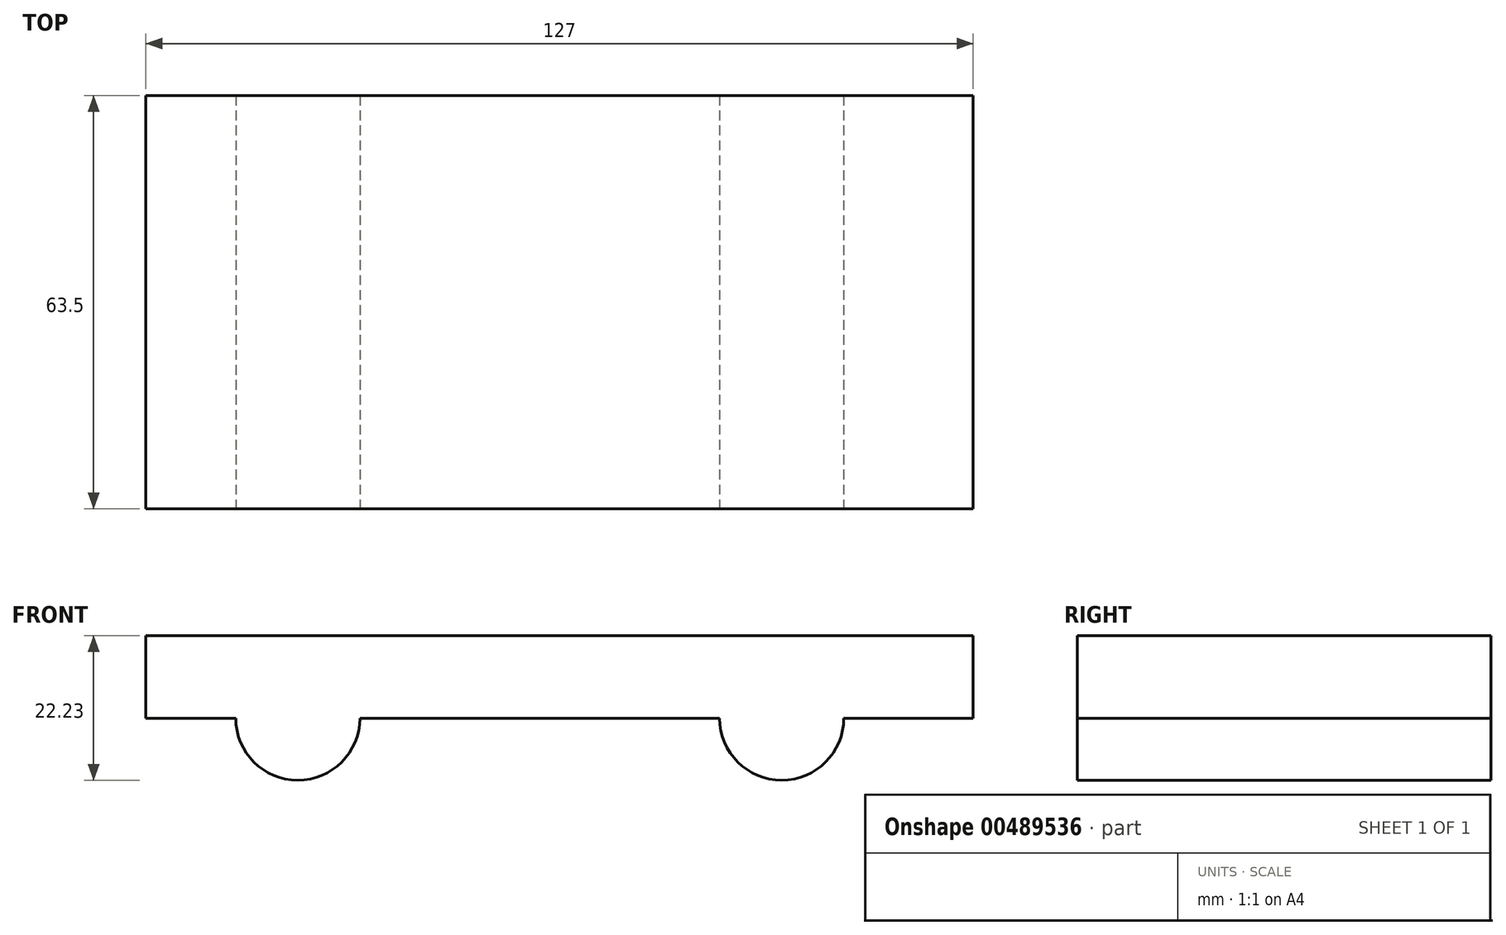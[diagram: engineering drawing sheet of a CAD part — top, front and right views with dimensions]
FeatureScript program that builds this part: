
annotation { "Feature Type Name" : "Feature", "Feature Type Description" : "" }
export const myFeature = defineFeature(function(context is Context, id is Id, definition is map)
    precondition{}
    {
        {
            var Q0;
            Q0=qCreatedBy(makeId("Top.planeOp"),FACE);
            var sketch = newSketch(context, id + "F0", { "sketchPlane" : qUnion([Q0])});
            skLineSegment(sketch, "E0.bottom", {"start": v(-63.5, 31.75) * mm, "end": v(63.5, 31.75) * mm});
            skLineSegment(sketch, "E0.top", {"start": v(-63.5, -31.75) * mm, "end": v(63.5, -31.75) * mm});
            skLineSegment(sketch, "E0.left", {"start": v(-63.5, 31.75) * mm, "end": v(-63.5, -31.75) * mm});
            skLineSegment(sketch, "E0.right", {"start": v(63.5, 31.75) * mm, "end": v(63.5, -31.75) * mm});
            skPoint(sketch, "E0.middle", {"position": v(0, 0) * mm});
            skSolve(sketch);
        }
        {
            var Q0;
            Q0=makeQuery(id+"F0.imprint","IMPRINT",FACE,{"disambiguationData":[TD([[makeQuery(id+"F0.imprint","IMPRINT",EDGE,{"derivedFrom":sQuery(id+"F0.wireOp",EDGE,"E0.bottom")}),-1.0]])]});
            extrude(context, id + "F1", {"entities" : qUnion([Q0]), "depth" : 12.7 * mm});
        }
        {
            var Q0;
            Q0=makeQuery(id+"F1.opExtrude","SWEPT_FACE",FACE,{"disambiguationData":[OSD([sQuery(id+"F0.wireOp",EDGE,"E0.top")])]});
            var sketch = newSketch(context, id + "F2", { "sketchPlane" : qUnion([Q0])});
            skCircle(sketch, "E1", {"center": v(-40.18, 0) * mm, "radius": 9.52 * mm});
            skSolve(sketch);
        }
        {
            var Q0;
            {var subQ0=sQuery(id+"F0.wireOp",EDGE,"E0.top");Q0=makeQuery(id+"F2.imprint","IMPRINT",FACE,{"disambiguationData":[TD([[makeQuery(id+"F2.imprint","IMPRINT",EDGE,{"derivedFrom":makeQuery(id+"F1.opExtrude","CAP_EDGE",EDGE,{"disambiguationData":[OSD([subQ0])],"isStart":false})}),-1.0]])]});}
            var sketch = newSketch(context, id + "F3", { "sketchPlane" : qUnion([Q0])});
            skCircle(sketch, "E2", {"center": v(34.1, 0) * mm, "radius": 9.53 * mm});
            skSolve(sketch);
        }
        {
            var Q0;
            {var subQ0=sQuery(id+"F2.wireOp",EDGE,"E1");var subQ1=makeQuery(id+"F1.opExtrude","CAP_EDGE",EDGE,{"disambiguationData":[OSD([sQuery(id+"F0.wireOp",EDGE,"E0.top")])],"isStart":true});var subQ2=makeQuery(id+"F2.imprint","INTERSECT",VERTEX,{"disambiguationData":[OD(0.0)],"derivedFrom":[subQ1,subQ0]});Q0=makeQuery(id+"F2.imprint","IMPRINT",FACE,{"disambiguationData":[TD([[makeQuery(id+"F2.imprint","IMPRINT",EDGE,{"disambiguationData":[TD([[subQ2,-1.0]])],"derivedFrom":subQ0}),1.0]])]});}
            var Q1;
            {var subQ0=sQuery(id+"F3.wireOp",EDGE,"E2");var subQ1=sQuery(id+"F0.wireOp",EDGE,"E0.top");var subQ2=makeQuery(id+"F1.opExtrude","CAP_EDGE",EDGE,{"disambiguationData":[OSD([subQ1])],"isStart":true});var subQ3=makeQuery(id+"F2.imprint","IMPRINT",EDGE,{"disambiguationData":[TD([[makeQuery(id+"F2.imprint","INTERSECT",VERTEX,{"disambiguationData":[OD(1.0)],"derivedFrom":[subQ2,sQuery(id+"F2.wireOp",EDGE,"E1")]}),-1.0]])],"derivedFrom":subQ2});var subQ4=makeQuery(id+"F3.imprint","INTERSECT",VERTEX,{"disambiguationData":[OD(0.0)],"derivedFrom":[subQ3,subQ0]});Q1=makeQuery(id+"F3.imprint","IMPRINT",FACE,{"disambiguationData":[TD([[makeQuery(id+"F3.imprint","IMPRINT",EDGE,{"disambiguationData":[TD([[subQ4,1.0]])],"derivedFrom":subQ0}),1.0]])]});}
            extrude(context, id + "F4", {"entities" : qUnion([Q0, Q1]), "operationType" : NewBodyOperationType.ADD, "oppositeDirection" : true, "depth" : 63.5 * mm});
        }
    });
